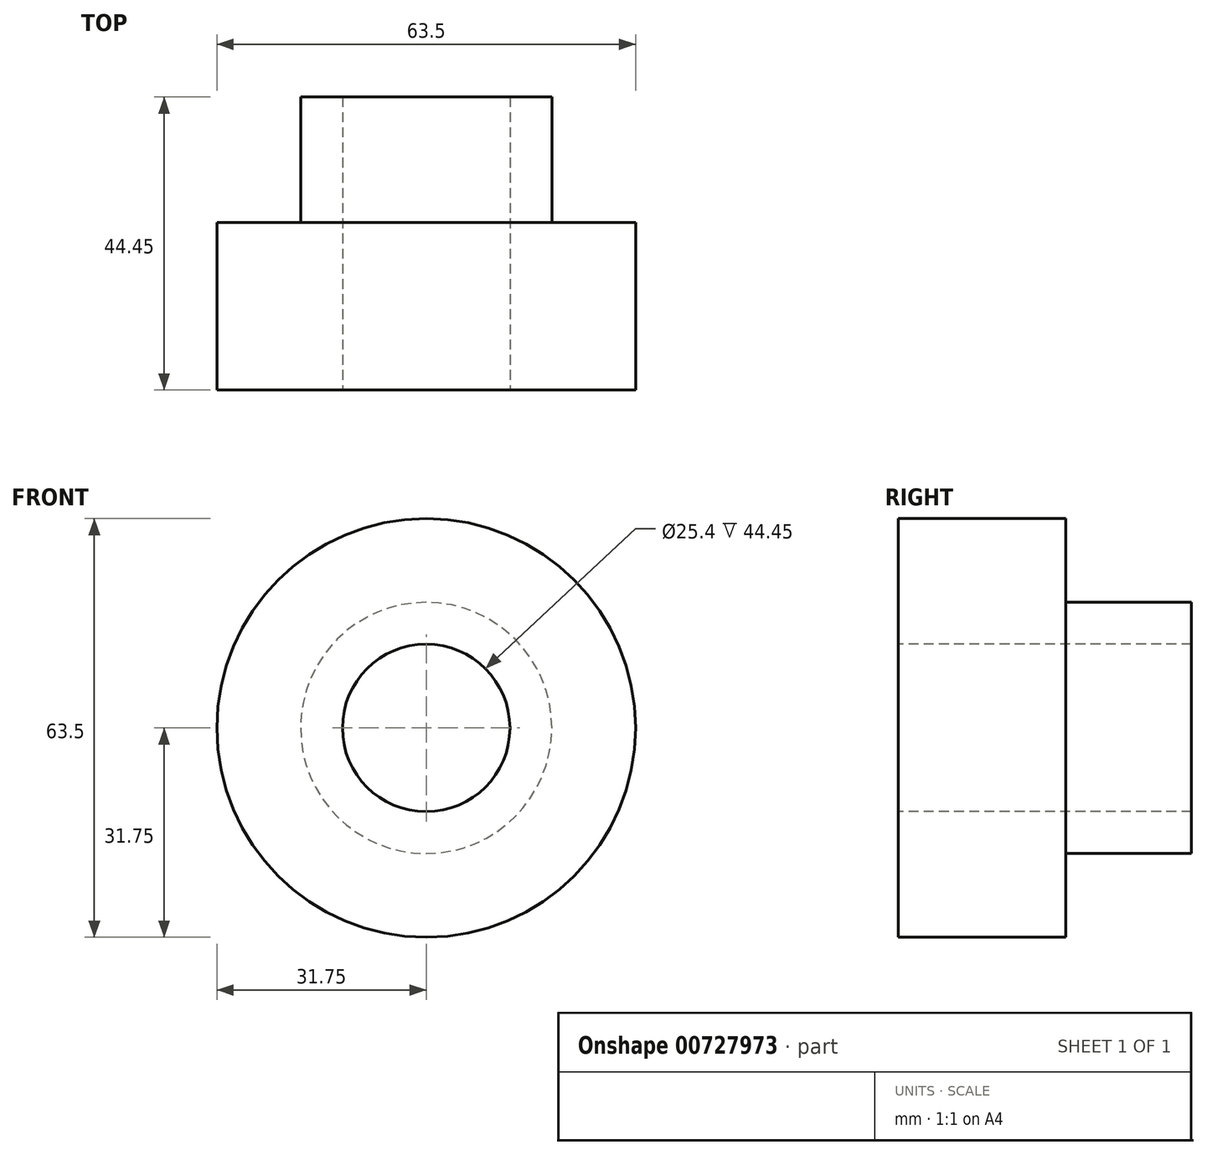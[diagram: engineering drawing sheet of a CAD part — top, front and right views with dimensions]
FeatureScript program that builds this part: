
annotation { "Feature Type Name" : "Feature", "Feature Type Description" : "" }
export const myFeature = defineFeature(function(context is Context, id is Id, definition is map)
    precondition{}
    {
        {
            var Q0;
            Q0=qCreatedBy(makeId("Front.planeOp"),FACE);
            var sketch = newSketch(context, id + "F0", { "sketchPlane" : qUnion([Q0])});
            skCircle(sketch, "E0", {"center": v(0, 0) * mm, "radius": 31.75 * mm});
            skSolve(sketch);
        }
        {
            var Q0;
            Q0=makeQuery(id+"F0.imprint","IMPRINT",FACE,{"disambiguationData":[TD([[makeQuery(id+"F0.imprint","IMPRINT",EDGE,{"derivedFrom":sQuery(id+"F0.wireOp",EDGE,"E0")}),1.0]])]});
            var sketch = newSketch(context, id + "F1", { "sketchPlane" : qUnion([Q0])});
            skCircle(sketch, "E1", {"center": v(0, 0) * mm, "radius": 19.05 * mm});
            skSolve(sketch);
        }
        {
            var Q0;
            Q0=makeQuery(id+"F1.imprint","IMPRINT",FACE,{"disambiguationData":[TD([[makeQuery(id+"F1.imprint","IMPRINT",EDGE,{"derivedFrom":sQuery(id+"F1.wireOp",EDGE,"E1")}),1.0]])]});
            var sketch = newSketch(context, id + "F2", { "sketchPlane" : qUnion([Q0])});
            skCircle(sketch, "E2", {"center": v(0, 0) * mm, "radius": 12.7 * mm});
            skSolve(sketch);
        }
        {
            var Q0;
            Q0=makeQuery(id+"F0.imprint","IMPRINT",FACE,{"disambiguationData":[TD([[makeQuery(id+"F0.imprint","IMPRINT",EDGE,{"derivedFrom":sQuery(id+"F0.wireOp",EDGE,"E0")}),1.0]])]});
            extrude(context, id + "F3", {"entities" : qUnion([Q0]), "depth" : 25.4 * mm, "offsetDistance" : 25.4 * mm});
        }
        {
            var Q0;
            Q0 = qSketchRegion(id + "F1", true);
            extrude(context, id + "F4", {"entities" : qUnion([Q0]), "operationType" : NewBodyOperationType.ADD, "oppositeDirection" : true, "depth" : 19.05 * mm, "offsetDistance" : 25.4 * mm});
        }
        {
            var Q0;
            Q0 = qSketchRegion(id + "F2", true);
            extrude(context, id + "F5", {"entities" : qUnion([Q0]), "operationType" : NewBodyOperationType.REMOVE, "oppositeDirection" : true, "depth" : 44.45 * mm, "offsetDistance" : 25.4 * mm});
        }
        {
            var Q0;
            Q0=makeQuery(id+"F5.boolean.opBoolean","COPY",FACE,{"derivedFrom":makeQuery(id+"F5.opExtrude","CAP_FACE",FACE,{"disambiguationData":[OSD([sQuery(id+"F2.wireOp",EDGE,"E2")])],"isStart":true})});
            extrude(context, id + "F6", {"entities" : qUnion([Q0]), "operationType" : NewBodyOperationType.REMOVE, "oppositeDirection" : true, "depth" : 25.4 * mm, "offsetDistance" : 25.4 * mm});
        }
    });
